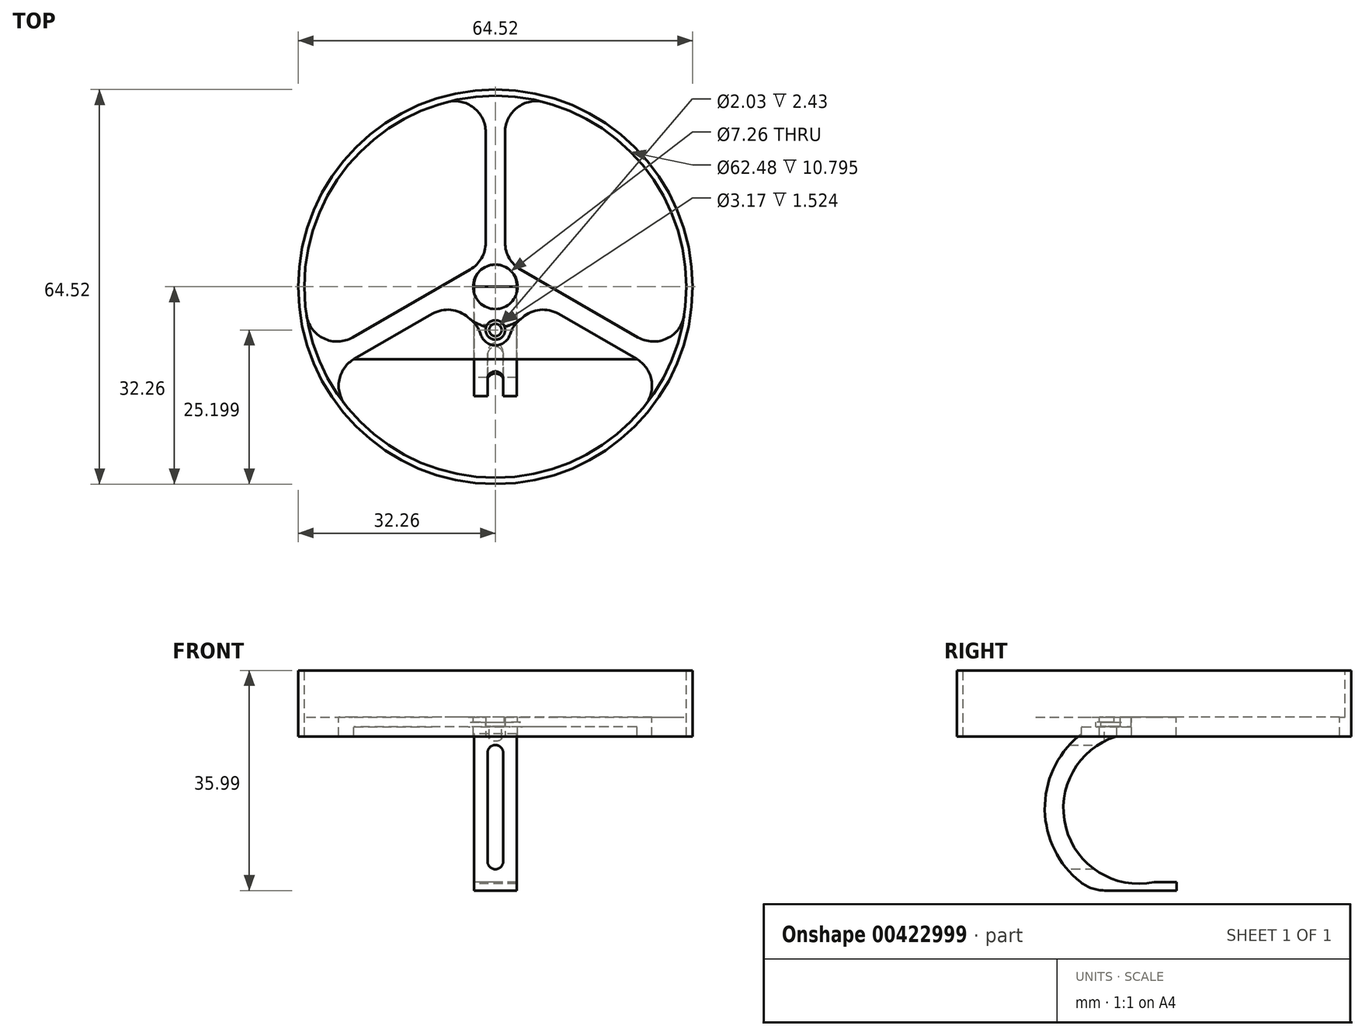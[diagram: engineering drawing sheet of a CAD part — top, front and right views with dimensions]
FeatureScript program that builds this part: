
annotation { "Feature Type Name" : "Feature", "Feature Type Description" : "" }
export const myFeature = defineFeature(function(context is Context, id is Id, definition is map)
    precondition{}
    {
        {
            var Q0;
            Q0=qCreatedBy(makeId("Top.planeOp"),FACE);
            var sketch = newSketch(context, id + "F0", { "sketchPlane" : qUnion([Q0])});
            skArc(sketch, "E0", {"start": v(2.25, 3.9) * mm, "mid": v(1.93, 4.08) * mm, "end": v(1.59, 4.22) * mm});
            skCircle(sketch, "E1", {"center": v(0, 0) * mm, "radius": 3.63 * mm});
            skCircle(sketch, "E2", {"center": v(0, 0) * mm, "radius": 32.26 * mm});
            skArc(sketch, "E3", {"start": v(-27.7, -14.45) * mm, "mid": v(0, -31.24) * mm, "end": v(27.7, -14.45) * mm});
            skLineSegment(sketch, "E4", {"start": v(2.25, 3.9) * mm, "end": v(29.03, -11.55) * mm});
            skLineSegment(sketch, "E5", {"start": v(-2.25, 3.9) * mm, "end": v(-29.03, -11.55) * mm});
            skArc(sketch, "E6.trimOffspring", {"start": v(29.03, -11.55) * mm, "mid": v(26.3, 16.87) * mm, "end": v(1.59, 31.2) * mm});
            skLineSegment(sketch, "E7", {"start": v(0, 14.05) * mm, "end": v(0, -14.19) * mm, "construction": true});
            skLineSegment(sketch, "E8", {"start": v(-23.16, -11.83) * mm, "end": v(23.16, -11.83) * mm});
            skLineSegment(sketch, "E9", {"start": v(-27.7, -14.45) * mm, "end": v(-23.16, -11.83) * mm});
            skLineSegment(sketch, "E10", {"start": v(27.7, -14.45) * mm, "end": v(23.16, -11.83) * mm});
            skLineSegment(sketch, "E11", {"start": v(-1.59, 4.22) * mm, "end": v(-1.59, 31.2) * mm});
            skLineSegment(sketch, "E12", {"start": v(1.59, 31.2) * mm, "end": v(1.59, 4.22) * mm});
            skArc(sketch, "E13.trimOffspring", {"start": v(-1.59, 31.2) * mm, "mid": v(-26.3, 16.87) * mm, "end": v(-29.03, -11.55) * mm});
            skArc(sketch, "E14.trimOffspring", {"start": v(-1.59, 4.22) * mm, "mid": v(-1.93, 4.08) * mm, "end": v(-2.25, 3.9) * mm});
            skSolve(sketch);
        }
        {
            var Q0;
            Q0 = qSketchRegion(id + "F0", true);
            extrude(context, id + "F1", {"entities" : qUnion([Q0]), "oppositeDirection" : true, "depth" : 3.17 * mm});
        }
        {
            var Q0;
            Q0=qCreatedBy(makeId("Right.planeOp"),FACE);
            cPlane(context, id + "F2", {"entities" : qUnion([Q0]), "cplaneType" : CPlaneType.OFFSET, "offset" : 0 * mm, "width" : 152.4 * mm, "height" : 152.4 * mm});
        }
        {
            var Q0;
            Q0=qCreatedBy(id+"F2.planeOp",FACE);
            var sketch = newSketch(context, id + "F3", { "sketchPlane" : qUnion([Q0])});
            skArc(sketch, "E15", {"start": v(-6.17, -3.18) * mm, "mid": v(-14.41, -18.02) * mm, "end": v(0, -27) * mm});
            skArc(sketch, "E16.0", {"start": v(-11.83, -2.73) * mm, "mid": v(-17.85, -14.83) * mm, "end": v(-11.99, -27) * mm});
            skLineSegment(sketch, "E17", {"start": v(0, -27) * mm, "end": v(3.73, -27) * mm});
            skLineSegment(sketch, "E18", {"start": v(3.73, -27) * mm, "end": v(3.73, -28.37) * mm});
            skLineSegment(sketch, "E19", {"start": v(3.73, -28.37) * mm, "end": v(-8.06, -28.37) * mm});
            skPoint(sketch, "E20.visualSharp", {"position": v(-9.94, -28.37) * mm});
            skArc(sketch, "E20.filletArc", {"start": v(-11.99, -27) * mm, "mid": v(-10.14, -28.02) * mm, "end": v(-8.06, -28.37) * mm});
            skLineSegment(sketch, "E21", {"start": v(-6.17, -3.18) * mm, "end": v(-6.17, -2.73) * mm});
            skLineSegment(sketch, "E22", {"start": v(-6.17, -2.73) * mm, "end": v(-11.83, -2.73) * mm});
            skSolve(sketch);
        }
        {
            var Q0;
            Q0 = qSketchRegion(id + "F3", true);
            extrude(context, id + "F4", {"entities" : qUnion([Q0]), "operationType" : NewBodyOperationType.ADD, "endBound" : BoundingType.SYMMETRIC, "depth" : 7 * mm});
        }
        {
            var Q0;
            Q0=qCreatedBy(makeId("Front.planeOp"),FACE);
            var sketch = newSketch(context, id + "F5", { "sketchPlane" : qUnion([Q0])});
            skLineSegment(sketch, "E23.bottom", {"start": v(1.27, -4.57) * mm, "end": v(-1.27, -4.57) * mm});
            skLineSegment(sketch, "E23.top", {"start": v(1.27, -24.9) * mm, "end": v(-1.27, -24.9) * mm});
            skLineSegment(sketch, "E23.left", {"start": v(1.27, -4.57) * mm, "end": v(1.27, -24.9) * mm});
            skLineSegment(sketch, "E23.right", {"start": v(-1.27, -4.57) * mm, "end": v(-1.27, -24.9) * mm});
            skSolve(sketch);
        }
        {
            var Q0;
            Q0 = qSketchRegion(id + "F5", true);
            extrude(context, id + "F6", {"entities" : qUnion([Q0]), "operationType" : NewBodyOperationType.REMOVE, "depth" : 25.4 * mm});
        }
        {
            var Q0;
            Q0=makeQuery(id+"F6.boolean.opBoolean","COPY",EDGE,{"derivedFrom":makeQuery(id+"F6.opExtrude","SWEPT_EDGE",EDGE,{"disambiguationData":[OSD([sQuery(id+"F5.wireOp",EDGE,"E23.bottom"),sQuery(id+"F5.wireOp",EDGE,"E23.left")])]})});
            var Q1;
            Q1=makeQuery(id+"F6.boolean.opBoolean","COPY",EDGE,{"derivedFrom":makeQuery(id+"F6.opExtrude","SWEPT_EDGE",EDGE,{"disambiguationData":[OSD([sQuery(id+"F5.wireOp",EDGE,"E23.bottom"),sQuery(id+"F5.wireOp",EDGE,"E23.right")])]})});
            var Q2;
            Q2=makeQuery(id+"F6.boolean.opBoolean","COPY",EDGE,{"derivedFrom":makeQuery(id+"F6.opExtrude","SWEPT_EDGE",EDGE,{"disambiguationData":[OSD([sQuery(id+"F5.wireOp",EDGE,"E23.top"),sQuery(id+"F5.wireOp",EDGE,"E23.left")])]})});
            var Q3;
            Q3=makeQuery(id+"F6.boolean.opBoolean","COPY",EDGE,{"derivedFrom":makeQuery(id+"F6.opExtrude","SWEPT_EDGE",EDGE,{"disambiguationData":[OSD([sQuery(id+"F5.wireOp",EDGE,"E23.top"),sQuery(id+"F5.wireOp",EDGE,"E23.right")])]})});
            fillet(context, id + "F7", {"entities" : qUnion([Q0, Q1, Q2, Q3]), "radius" : 1.27 * mm, "tangentPropagation" : true, "allowEdgeOverflow" : false});
        }
        {
            var Q0;
            Q0=makeQuery(id+"F4.opExtrude","CAP_EDGE",EDGE,{"disambiguationData":[OSD([sQuery(id+"F3.wireOp",EDGE,"E18")])],"isStart":true});
            var Q1;
            Q1=makeQuery(id+"F4.opExtrude","CAP_EDGE",EDGE,{"disambiguationData":[OSD([sQuery(id+"F3.wireOp",EDGE,"E18")])],"isStart":false});
            fillet(context, id + "F8", {"entities" : qUnion([Q0, Q1]), "radius" : 3.48 * mm, "tangentPropagation" : true, "allowEdgeOverflow" : false});
        }
        {
            var Q0;
            Q0=makeQuery(id+"F1.opExtrude","CAP_FACE",FACE,{"disambiguationData":[OSD([sQuery(id+"F0.wireOp",EDGE,"E0"),sQuery(id+"F0.wireOp",EDGE,"E1"),sQuery(id+"F0.wireOp",EDGE,"E2"),sQuery(id+"F0.wireOp",EDGE,"E3"),sQuery(id+"F0.wireOp",EDGE,"E4"),sQuery(id+"F0.wireOp",EDGE,"3Kbo6qPl-UeJc-SpGb-QunT-igpGF68ZOVeu"),sQuery(id+"F0.wireOp",EDGE,"E5"),sQuery(id+"F0.wireOp",EDGE,"UkC3B4rK-ZQAm-ILdF-c06i-0da9ncZ2dpg8"),sQuery(id+"F0.wireOp",EDGE,"E6.trimOffspring"),sQuery(id+"F0.wireOp",EDGE,"E8")])],"isStart":true});
            var sketch = newSketch(context, id + "F9", { "sketchPlane" : qUnion([Q0])});
            skCircle(sketch, "E24", {"center": v(0, 0) * mm, "radius": 32.26 * mm});
            skCircle(sketch, "E25", {"center": v(0, 0) * mm, "radius": 31.24 * mm});
            skSolve(sketch);
        }
        {
            var Q0;
            Q0 = qSketchRegion(id + "F9", true);
            extrude(context, id + "F10", {"entities" : qUnion([Q0]), "operationType" : NewBodyOperationType.ADD, "depth" : 7.62 * mm});
        }
        {
            var Q0;
            Q0=makeQuery(id+"F1.opExtrude","CAP_FACE",FACE,{"disambiguationData":[OSD([sQuery(id+"F0.wireOp",EDGE,"E0"),sQuery(id+"F0.wireOp",EDGE,"E1"),sQuery(id+"F0.wireOp",EDGE,"E2"),sQuery(id+"F0.wireOp",EDGE,"E4"),sQuery(id+"F0.wireOp",EDGE,"E5"),sQuery(id+"F0.wireOp",EDGE,"E8"),sQuery(id+"F0.wireOp",EDGE,"E9"),sQuery(id+"F0.wireOp",EDGE,"E10"),sQuery(id+"F0.wireOp",EDGE,"E6.trimOffspring"),sQuery(id+"F0.wireOp",EDGE,"E3"),sQuery(id+"F0.wireOp",EDGE,"E11"),sQuery(id+"F0.wireOp",EDGE,"E12"),sQuery(id+"F0.wireOp",EDGE,"E13.trimOffspring"),sQuery(id+"F0.wireOp",EDGE,"E14.trimOffspring")])],"isStart":true});
            var sketch = newSketch(context, id + "F11", { "sketchPlane" : qUnion([Q0])});
            skLineSegment(sketch, "E26", {"start": v(-23.16, -11.83) * mm, "end": v(-6.35, -2.13) * mm});
            skLineSegment(sketch, "E27", {"start": v(-23.16, -13.73) * mm, "end": v(-23.16, -11.83) * mm});
            skLineSegment(sketch, "E28", {"start": v(23.16, -11.83) * mm, "end": v(6.35, -2.13) * mm});
            skLineSegment(sketch, "E29", {"start": v(23.16, -13.9) * mm, "end": v(23.16, -11.83) * mm});
            skArc(sketch, "E30", {"start": v(-6.35, -2.13) * mm, "mid": v(0, -6.7) * mm, "end": v(6.35, -2.13) * mm});
            skLineSegment(sketch, "E31", {"start": v(-23.16, -13.73) * mm, "end": v(23.16, -13.9) * mm});
            skSolve(sketch);
        }
        {
            var Q0;
            Q0 = qSketchRegion(id + "F11", true);
            extrude(context, id + "F12", {"entities" : qUnion([Q0]), "operationType" : NewBodyOperationType.REMOVE, "oppositeDirection" : true, "depth" : 1.57 * mm});
        }
        {
            var Q0;
            Q0=makeQuery(id+"F1.opExtrude","SWEPT_EDGE",EDGE,{"disambiguationData":[OSD([sQuery(id+"F0.wireOp",EDGE,"E0"),sQuery(id+"F0.wireOp",EDGE,"E12")])]});
            var Q1;
            Q1=makeQuery(id+"F1.opExtrude","SWEPT_EDGE",EDGE,{"disambiguationData":[OSD([sQuery(id+"F0.wireOp",EDGE,"E11"),sQuery(id+"F0.wireOp",EDGE,"E14.trimOffspring")])]});
            var Q2;
            Q2=makeQuery(id+"F12.boolean.opBoolean","COPY",EDGE,{"derivedFrom":makeQuery(id+"F12.opExtrude","SWEPT_EDGE",EDGE,{"disambiguationData":[OSD([sQuery(id+"F11.wireOp",EDGE,"E28"),sQuery(id+"F11.wireOp",EDGE,"E30")])]})});
            var Q3;
            Q3=makeQuery(id+"F12.boolean.opBoolean","COPY",EDGE,{"derivedFrom":makeQuery(id+"F12.opExtrude","SWEPT_EDGE",EDGE,{"disambiguationData":[OSD([sQuery(id+"F11.wireOp",EDGE,"E26"),sQuery(id+"F11.wireOp",EDGE,"E30")])]})});
            var Q4;
            Q4=makeQuery(id+"F1.opExtrude","SWEPT_EDGE",EDGE,{"disambiguationData":[OSD([sQuery(id+"F0.wireOp",EDGE,"E6.trimOffspring"),sQuery(id+"F0.wireOp",EDGE,"E12")])]});
            var Q5;
            Q5=makeQuery(id+"F1.opExtrude","SWEPT_EDGE",EDGE,{"disambiguationData":[OSD([sQuery(id+"F0.wireOp",EDGE,"E11"),sQuery(id+"F0.wireOp",EDGE,"E13.trimOffspring")])]});
            var Q6;
            Q6=makeQuery(id+"F1.opExtrude","SWEPT_EDGE",EDGE,{"disambiguationData":[OSD([sQuery(id+"F0.wireOp",EDGE,"E9"),sQuery(id+"F0.wireOp",EDGE,"E3")])]});
            var Q7;
            Q7=makeQuery(id+"F1.opExtrude","SWEPT_EDGE",EDGE,{"disambiguationData":[OSD([sQuery(id+"F0.wireOp",EDGE,"E5"),sQuery(id+"F0.wireOp",EDGE,"E13.trimOffspring")])]});
            var Q8;
            Q8=makeQuery(id+"F1.opExtrude","SWEPT_EDGE",EDGE,{"disambiguationData":[OSD([sQuery(id+"F0.wireOp",EDGE,"E10"),sQuery(id+"F0.wireOp",EDGE,"E3")])]});
            var Q9;
            Q9=makeQuery(id+"F1.opExtrude","SWEPT_EDGE",EDGE,{"disambiguationData":[OSD([sQuery(id+"F0.wireOp",EDGE,"E4"),sQuery(id+"F0.wireOp",EDGE,"E6.trimOffspring")])]});
            fillet(context, id + "F13", {"entities" : qUnion([Q0, Q1, Q2, Q3, Q4, Q5, Q6, Q7, Q8, Q9]), "radius" : 5.08 * mm, "tangentPropagation" : true, "allowEdgeOverflow" : false});
        }
        {
            var Q0;
            Q0=makeQuery(id+"F12.boolean.opBoolean","COPY",FACE,{"derivedFrom":makeQuery(id+"F12.opExtrude","CAP_FACE",FACE,{"disambiguationData":[OSD([sQuery(id+"F11.wireOp",EDGE,"E26"),sQuery(id+"F11.wireOp",EDGE,"E27"),sQuery(id+"F11.wireOp",EDGE,"E28"),sQuery(id+"F11.wireOp",EDGE,"E29"),sQuery(id+"F11.wireOp",EDGE,"E30"),sQuery(id+"F11.wireOp",EDGE,"E31")])],"isStart":false})});
            var sketch = newSketch(context, id + "F14", { "sketchPlane" : qUnion([Q0])});
            skCircle(sketch, "E32", {"center": v(0, -7.06) * mm, "radius": 2.5 * mm});
            skPoint(sketch, "E32.centerSnap0", {"position": v(0, -6.7) * mm});
            skSolve(sketch);
        }
        {
            var Q0;
            Q0 = qSketchRegion(id + "F14", true);
            extrude(context, id + "F15", {"entities" : qUnion([Q0]), "operationType" : NewBodyOperationType.ADD, "depth" : 0.76 * mm});
        }
        {
            var Q0;
            Q0=makeQuery(id+"F15.boolean.opBoolean","INTERSECT",EDGE,{"disambiguationData":[OD(0.0)],"derivedFrom":[makeQuery(id+"F12.boolean.opBoolean","COPY",FACE,{"derivedFrom":makeQuery(id+"F12.opExtrude","SWEPT_FACE",FACE,{"disambiguationData":[OSD([sQuery(id+"F11.wireOp",EDGE,"E30")])]})}),makeQuery(id+"F15.opExtrude","SWEPT_FACE",FACE,{"disambiguationData":[OSD([sQuery(id+"F14.wireOp",EDGE,"E32")])]})]});
            var Q1;
            Q1=makeQuery(id+"F15.boolean.opBoolean","INTERSECT",EDGE,{"disambiguationData":[OD(1.0)],"derivedFrom":[makeQuery(id+"F12.boolean.opBoolean","COPY",FACE,{"derivedFrom":makeQuery(id+"F12.opExtrude","SWEPT_FACE",FACE,{"disambiguationData":[OSD([sQuery(id+"F11.wireOp",EDGE,"E30")])]})}),makeQuery(id+"F15.opExtrude","SWEPT_FACE",FACE,{"disambiguationData":[OSD([sQuery(id+"F14.wireOp",EDGE,"E32")])]})]});
            fillet(context, id + "F16", {"entities" : qUnion([Q0, Q1]), "radius" : 5.08 * mm, "tangentPropagation" : true, "allowEdgeOverflow" : false});
        }
        {
            var Q0;
            Q0=makeQuery(id+"F1.opExtrude","CAP_FACE",FACE,{"disambiguationData":[OSD([sQuery(id+"F0.wireOp",EDGE,"E0"),sQuery(id+"F0.wireOp",EDGE,"E1"),sQuery(id+"F0.wireOp",EDGE,"E2"),sQuery(id+"F0.wireOp",EDGE,"E4"),sQuery(id+"F0.wireOp",EDGE,"E5"),sQuery(id+"F0.wireOp",EDGE,"E8"),sQuery(id+"F0.wireOp",EDGE,"E9"),sQuery(id+"F0.wireOp",EDGE,"E10"),sQuery(id+"F0.wireOp",EDGE,"E6.trimOffspring"),sQuery(id+"F0.wireOp",EDGE,"E3"),sQuery(id+"F0.wireOp",EDGE,"E11"),sQuery(id+"F0.wireOp",EDGE,"E12"),sQuery(id+"F0.wireOp",EDGE,"E13.trimOffspring"),sQuery(id+"F0.wireOp",EDGE,"E14.trimOffspring")])],"isStart":true});
            var sketch = newSketch(context, id + "F17", { "sketchPlane" : qUnion([Q0])});
            skCircle(sketch, "E33", {"center": v(0, -7.06) * mm, "radius": 1.02 * mm});
            skPoint(sketch, "E33.centerSnap0", {"position": v(0, -6.7) * mm});
            skSolve(sketch);
        }
        {
            var Q0;
            Q0 = qSketchRegion(id + "F17", true);
            extrude(context, id + "F18", {"entities" : qUnion([Q0]), "operationType" : NewBodyOperationType.REMOVE, "oppositeDirection" : true, "depth" : 25.4 * mm});
        }
        {
            var Q0;
            Q0=makeQuery(id+"F1.opExtrude","CAP_FACE",FACE,{"disambiguationData":[OSD([sQuery(id+"F0.wireOp",EDGE,"E0"),sQuery(id+"F0.wireOp",EDGE,"E1"),sQuery(id+"F0.wireOp",EDGE,"E2"),sQuery(id+"F0.wireOp",EDGE,"E4"),sQuery(id+"F0.wireOp",EDGE,"E5"),sQuery(id+"F0.wireOp",EDGE,"E8"),sQuery(id+"F0.wireOp",EDGE,"E9"),sQuery(id+"F0.wireOp",EDGE,"E10"),sQuery(id+"F0.wireOp",EDGE,"E6.trimOffspring"),sQuery(id+"F0.wireOp",EDGE,"E3"),sQuery(id+"F0.wireOp",EDGE,"E11"),sQuery(id+"F0.wireOp",EDGE,"E12"),sQuery(id+"F0.wireOp",EDGE,"E13.trimOffspring"),sQuery(id+"F0.wireOp",EDGE,"E14.trimOffspring")])],"isStart":true});
            var sketch = newSketch(context, id + "F19", { "sketchPlane" : qUnion([Q0])});
            skCircle(sketch, "E34", {"center": v(0, -7.06) * mm, "radius": 1.59 * mm});
            skSolve(sketch);
        }
        {
            var Q0;
            Q0 = qSketchRegion(id + "F19", true);
            extrude(context, id + "F20", {"entities" : qUnion([Q0]), "operationType" : NewBodyOperationType.REMOVE, "oppositeDirection" : true, "depth" : 1.52 * mm});
        }
    });
